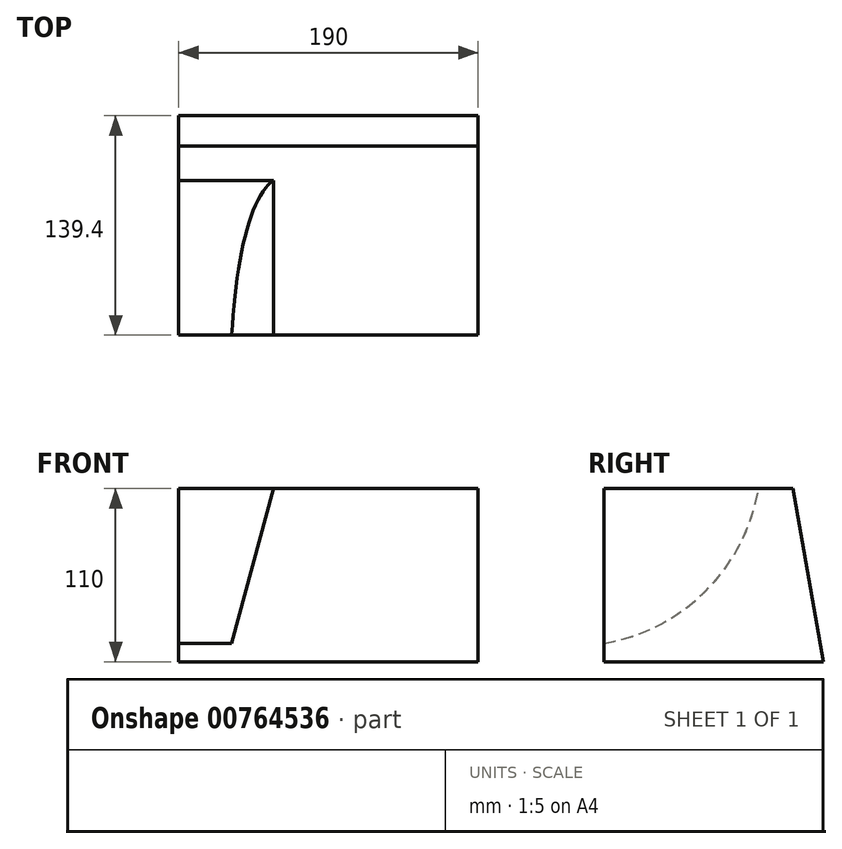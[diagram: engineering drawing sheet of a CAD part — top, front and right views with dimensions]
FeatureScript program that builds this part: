
annotation { "Feature Type Name" : "Feature", "Feature Type Description" : "" }
export const myFeature = defineFeature(function(context is Context, id is Id, definition is map)
    precondition{}
    {
        {
            var Q0;
            Q0=qCreatedBy(makeId("Top.planeOp"),FACE);
            var sketch = newSketch(context, id + "F0", { "sketchPlane" : qUnion([Q0])});
            skLineSegment(sketch, "E0.bottom", {"start": v(95, 60) * mm, "end": v(-95, 60) * mm});
            skLineSegment(sketch, "E0.top", {"start": v(95, -60) * mm, "end": v(-95, -60) * mm});
            skLineSegment(sketch, "E0.left", {"start": v(95, 60) * mm, "end": v(95, -60) * mm});
            skLineSegment(sketch, "E0.right", {"start": v(-95, 60) * mm, "end": v(-95, -60) * mm});
            skPoint(sketch, "E0.middle", {"position": v(0, 0) * mm});
            skSolve(sketch);
        }
        {
            var Q0;
            Q0=makeQuery(id+"F0.imprint","IMPRINT",FACE,{"disambiguationData":[TD([[makeQuery(id+"F0.imprint","IMPRINT",EDGE,{"derivedFrom":sQuery(id+"F0.wireOp",EDGE,"E0.bottom")}),1.0]])]});
            extrude(context, id + "F1", {"entities" : qUnion([Q0]), "oppositeDirection" : true, "depth" : 110 * mm, "offsetDistance" : 25 * mm});
        }
        {
            var Q0;
            Q0=makeQuery(id+"F1.opExtrude","SWEPT_FACE",FACE,{"disambiguationData":[OSD([sQuery(id+"F0.wireOp",EDGE,"E0.left")])]});
            var sketch = newSketch(context, id + "F2", { "sketchPlane" : qUnion([Q0])});
            skLineSegment(sketch, "E1.0.0", {"start": v(-60, 0) * mm, "end": v(60, 0) * mm});
            skLineSegment(sketch, "E1.0.1", {"start": v(60, 0) * mm, "end": v(60, -110) * mm});
            skLineSegment(sketch, "E1.0.2", {"start": v(60, -110) * mm, "end": v(-60, -110) * mm});
            skLineSegment(sketch, "E1.0.3", {"start": v(-60, -110) * mm, "end": v(-60, 0) * mm});
            skLineSegment(sketch, "E2", {"start": v(60, 0) * mm, "end": v(-60, 0) * mm});
            skLineSegment(sketch, "E3", {"start": v(-60, -110) * mm, "end": v(60, -110) * mm});
            skLineSegment(sketch, "E4", {"start": v(60, -110) * mm, "end": v(151, -110) * mm});
            skLineSegment(sketch, "E5", {"start": v(-60, -110) * mm, "end": v(-60, -60) * mm});
            skLineSegment(sketch, "E6", {"start": v(-60, -60) * mm, "end": v(60, 0) * mm});
            skLineSegment(sketch, "E7", {"start": v(60, 0) * mm, "end": v(93.13, -187.88) * mm});
            skSolve(sketch);
        }
        {
            var Q0;
            {var subQ0=sQuery(id+"F2.wireOp",EDGE,"E1.0.1");Q0=makeQuery(id+"F2.imprint","IMPRINT",FACE,{"disambiguationData":[TD([[makeQuery(id+"F2.imprint","IMPRINT",EDGE,{"derivedFrom":subQ0}),-1.0]])]});}
            var Q1;
            Q1=makeQuery(id+"F1.opExtrude","SWEPT_FACE",FACE,{"disambiguationData":[OSD([sQuery(id+"F0.wireOp",EDGE,"E0.right")])]});
            extrude(context, id + "F3", {"entities" : qUnion([Q0]), "operationType" : NewBodyOperationType.ADD, "endBound" : BoundingType.UP_TO_SURFACE, "oppositeDirection" : true, "depth" : 25 * mm, "endBoundEntityFace" : qUnion([Q1]), "offsetDistance" : 25 * mm});
        }
        {
            var Q0;
            {var subQ0=sQuery(id+"F0.wireOp",EDGE,"E0.right");Q0=makeQuery(id+"F3.boolean.opBoolean","MERGE",FACE,{"derivedFrom":[makeQuery(id+"F1.opExtrude","SWEPT_FACE",FACE,{"disambiguationData":[OSD([subQ0])]}),makeQuery(id+"F3.opExtrude","CAP_FACE",FACE,{"disambiguationData":[OSD([subQ0])],"isStart":false})]});}
            var sketch = newSketch(context, id + "F4", { "sketchPlane" : qUnion([Q0])});
            skLineSegment(sketch, "E8.0.0", {"start": v(60, 0) * mm, "end": v(-60, 0) * mm});
            skLineSegment(sketch, "E8.0.1", {"start": v(-60, 0) * mm, "end": v(-79.4, -110) * mm});
            skLineSegment(sketch, "E8.0.2", {"start": v(-79.4, -110) * mm, "end": v(60, -110) * mm});
            skLineSegment(sketch, "E8.0.3", {"start": v(60, -110) * mm, "end": v(60, 0) * mm});
            skLineSegment(sketch, "E9", {"start": v(60, 0) * mm, "end": v(60, 20) * mm});
            skLineSegment(sketch, "E10", {"start": v(60, 20) * mm, "end": v(80, 20) * mm});
            skCircle(sketch, "E11", {"center": v(80, 20) * mm, "radius": 120 * mm});
            skSolve(sketch);
        }
        {
            var Q0;
            Q0=makeQuery(id+"F1.opExtrude","CAP_FACE",FACE,{"disambiguationData":[OSD([sQuery(id+"F0.wireOp",EDGE,"E0.bottom"),sQuery(id+"F0.wireOp",EDGE,"E0.top"),sQuery(id+"F0.wireOp",EDGE,"E0.left"),sQuery(id+"F0.wireOp",EDGE,"E0.right")])],"isStart":true});
            var sketch = newSketch(context, id + "F5", { "sketchPlane" : qUnion([Q0])});
            skLineSegment(sketch, "E12.0", {"start": v(95, 60) * mm, "end": v(-95, 60) * mm});
            skLineSegment(sketch, "E13", {"start": v(-95, 60) * mm, "end": v(-35, 60) * mm});
            skLineSegment(sketch, "E14", {"start": v(-35, 60) * mm, "end": v(-35, -60) * mm});
            skSolve(sketch);
        }
        {
            var Q0;
            Q0=sQuery(id+"F5.wireOp",EDGE,"E14");
            cPlane(context, id + "F6", {"entities" : qUnion([Q0]), "cplaneType" : CPlaneType.LINE_ANGLE, "offset" : 25 * mm, "angle" : 75 * degree, "width" : 150 * mm, "height" : 150 * mm});
        }
        {
            var Q0;
            {var subQ0=sQuery(id+"F4.wireOp",EDGE,"E8.0.3");var subQ1=sQuery(id+"F4.wireOp",EDGE,"E8.0.0");var subQ2=makeQuery(id+"F4.imprint","INTERSECT",VERTEX,{"derivedFrom":[subQ1,subQ0]});Q0=makeQuery(id+"F4.imprint","IMPRINT",FACE,{"disambiguationData":[TD([[makeQuery(id+"F4.imprint","IMPRINT",EDGE,{"disambiguationData":[TD([[subQ2,1.0]])],"derivedFrom":subQ1}),-1.0]])]});}
            var Q1;
            Q1=qCreatedBy(id+"F6.planeOp",FACE);
            extrude(context, id + "F7", {"entities" : qUnion([Q0]), "operationType" : NewBodyOperationType.REMOVE, "endBound" : BoundingType.UP_TO_SURFACE, "oppositeDirection" : true, "depth" : 25 * mm, "endBoundEntityFace" : qUnion([Q1]), "offsetDistance" : 25 * mm});
        }
    });
